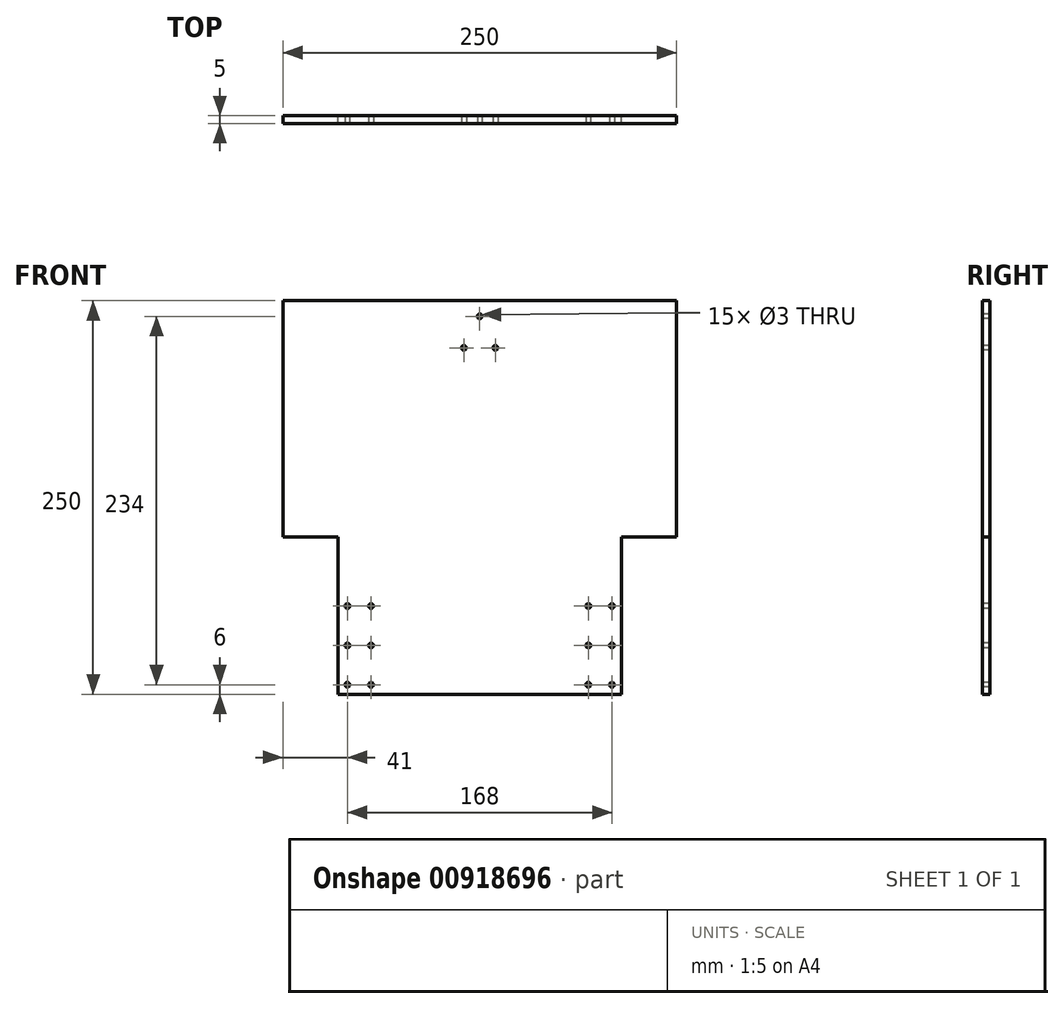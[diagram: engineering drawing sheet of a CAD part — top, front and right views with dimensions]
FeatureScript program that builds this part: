
annotation { "Feature Type Name" : "Feature", "Feature Type Description" : "" }
export const myFeature = defineFeature(function(context is Context, id is Id, definition is map)
    precondition{}
    {
        {
            var Q0;
            Q0=qCreatedBy(makeId("Front.planeOp"),FACE);
            var sketch = newSketch(context, id + "F0", { "sketchPlane" : qUnion([Q0])});
            skLineSegment(sketch, "E0.bottom", {"start": v(125, -75) * mm, "end": v(90, -75) * mm});
            skLineSegment(sketch, "E0.top", {"start": v(125, 75) * mm, "end": v(-125, 75) * mm});
            skLineSegment(sketch, "E0.left", {"start": v(125, -75) * mm, "end": v(125, 75) * mm});
            skLineSegment(sketch, "E0.right", {"start": v(-125, -75) * mm, "end": v(-125, 75) * mm});
            skPoint(sketch, "E0.middle", {"position": v(0, 0) * mm});
            skLineSegment(sketch, "E1.bottom", {"start": v(90, -175) * mm, "end": v(-90, -175) * mm});
            skLineSegment(sketch, "E1.left", {"start": v(90, -175) * mm, "end": v(90, -75) * mm});
            skLineSegment(sketch, "E1.right", {"start": v(-90, -175) * mm, "end": v(-90, -75) * mm});
            skLineSegment(sketch, "E2.trimOffspring", {"start": v(-90, -75) * mm, "end": v(-125, -75) * mm});
            skSolve(sketch);
        }
        {
            var Q0;
            Q0=makeQuery(id+"F0.imprint","IMPRINT",FACE,{"disambiguationData":[TD([[makeQuery(id+"F0.imprint","IMPRINT",EDGE,{"derivedFrom":sQuery(id+"F0.wireOp",EDGE,"E0.bottom")}),-1.0]])]});
            extrude(context, id + "F1", {"entities" : qUnion([Q0]), "depth" : 5 * mm, "offsetDistance" : 25 * mm});
        }
        {
            var Q0;
            Q0=makeQuery(id+"F1.opExtrude","CAP_FACE",FACE,{"disambiguationData":[OSD([sQuery(id+"F0.wireOp",EDGE,"E0.bottom"),sQuery(id+"F0.wireOp",EDGE,"E0.top"),sQuery(id+"F0.wireOp",EDGE,"E0.left"),sQuery(id+"F0.wireOp",EDGE,"E0.right"),sQuery(id+"F0.wireOp",EDGE,"E1.bottom"),sQuery(id+"F0.wireOp",EDGE,"E1.left"),sQuery(id+"F0.wireOp",EDGE,"E1.right"),sQuery(id+"F0.wireOp",EDGE,"E2.trimOffspring")])],"isStart":false});
            var sketch = newSketch(context, id + "F2", { "sketchPlane" : qUnion([Q0])});
            skCircle(sketch, "E3", {"center": v(0, 65) * mm, "radius": 1.5 * mm});
            skCircle(sketch, "E4", {"center": v(-10, 45) * mm, "radius": 1.5 * mm});
            skCircle(sketch, "E5", {"center": v(10, 45) * mm, "radius": 1.5 * mm});
            skCircle(sketch, "E6", {"center": v(-84, -169) * mm, "radius": 1.5 * mm});
            skCircle(sketch, "E7.0.1.0", {"center": v(-84, -144) * mm, "radius": 1.5 * mm});
            skCircle(sketch, "E7.0.2.0", {"center": v(-84, -119) * mm, "radius": 1.5 * mm});
            skCircle(sketch, "E7.1.0.0", {"center": v(-69, -169) * mm, "radius": 1.5 * mm});
            skCircle(sketch, "E7.1.1.0", {"center": v(-69, -144) * mm, "radius": 1.5 * mm});
            skCircle(sketch, "E7.1.2.0", {"center": v(-69, -119) * mm, "radius": 1.5 * mm});
            skCircle(sketch, "E8.MirrorC", {"center": v(84, -169) * mm, "radius": 1.5 * mm});
            skCircle(sketch, "E9.MirrorC", {"center": v(84, -144) * mm, "radius": 1.5 * mm});
            skCircle(sketch, "E10.MirrorC", {"center": v(69, -169) * mm, "radius": 1.5 * mm});
            skCircle(sketch, "E11.MirrorC", {"center": v(69, -119) * mm, "radius": 1.5 * mm});
            skCircle(sketch, "E12.MirrorC", {"center": v(69, -144) * mm, "radius": 1.5 * mm});
            skCircle(sketch, "E13.MirrorC", {"center": v(84, -119) * mm, "radius": 1.5 * mm});
            skSolve(sketch);
        }
        {
            var Q0;
            Q0 = qSketchRegion(id + "F2", true);
            extrude(context, id + "F3", {"entities" : qUnion([Q0]), "operationType" : NewBodyOperationType.REMOVE, "oppositeDirection" : true, "depth" : 5 * mm, "offsetDistance" : 25 * mm});
        }
    });
